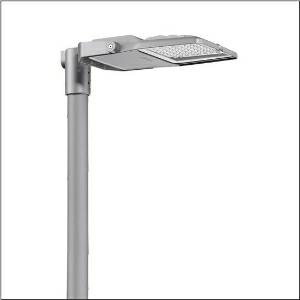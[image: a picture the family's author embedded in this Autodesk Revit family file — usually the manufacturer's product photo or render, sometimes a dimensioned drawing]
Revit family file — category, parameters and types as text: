
# Revit family: floodlight_fl_21_iq_mini___pl43_5xa7772c4a3a_a38e
name_source: partatom
category: Lighting Fixtures
units: mm (PartAtom-declared; Revit-internal decimal feet)

## family parameters
Cut with Voids When Loaded = No
Host = Face
Light Source = No
Part Type = Normal
Room Calculation Point = No
Round Connector Dimension = Use Diameter
Shared = No

## types (1)
- --- (1 x LED, 13050 lm, 87.2 W, 4000K)
    Apparent Load = 87 VA
    CIE Flux Codes = 27 78 99 100 100
    Color Rendering = 70
    Color Temperature = 4000K
    Default Elevation = 1800 mm
    Description = Floodlight FL 21 iQ mini, floodlight, primary light control with lens, of PMMA, primary optical cover: protective disc, of toughened safety glass, transparent, light distribution: PL43, light emission: direct distribution, installation type: surface-mounted, LED, High Power LED, rated luminous flux: 13.050lm, luminous efficacy: 150lm/W, light colour: 740, colour temperature: 4000K, control gear: iQ Street-Remote/DALI, control: Auto-Match, Temp-Guard, Night-Set, Smart-Wire, Desk-Remote (wireless, voltage-free reading and setting of iQ features in the workshop via application-optimized NFC function/RFID function), optimised constant luminous flux control (CLO 2.0), Light-Fading, Lumen-Switch, with terminal, 6-pole, mains connection: 220..240V, AC, 50/60Hz, start of lifetime: 87W, end of service life: 92W, reduction: 40W, luminaire housing, of diecast aluminium, powder-coated, Siteco® metallic grey (DB 702S), corrosivity category C5 mid according to DIN EN ISO 12944, suitable for swimming pools, chlorine-resistant, sealing non-destructively replaceable, please order mast flange separately, mast bracket, of steel, galvanised, powder-coated, protection rating (complete): IP66, insulation class (complete): insulation class II (safety insulation), certification: CE, ENEC, VDE, protection symbol: D, impact resistance: IK08, permissible operating ambient temperature: -40..+40°C, permissible operating ambient temperature for outdoor applications: -40..+50°C, standard: DIN EN 12944, LABS conformity tested according to VDMA 24364:2018-05, packaging unit: 1 piece

Light Distribution: PL43
    Height = 70 mm
    Lamp = 1 x LED
    Lamp Light Flux = 13050 lm
    Lamp Power = 87.2 W
    Lamp count = 1
    Length = 485 mm
    Luminous efficacy = 150 lm/W
    Manufacturer = Siteco
    ModVariant = No
    Model = 5XA7772C4A3A
    Number of Poles = 1
    OnlyDefault = Yes
    Power Factor = 1
    Product Name = Floodlight FL 21 iQ mini | PL43
    Product group = floodlight | pylon annexe
    ProductGroupID = 6200
    Protection Class = Protection class II
    Protection Degree = IP 66
    RLX_Detail_Level = 1
    RLX_Emergency_Light_Flux = 0 lm
    RLX_Emergency_Type = 0
    RLX_Emergency_Type_DB = No
    RlxData = <blob elided: 101397 chars, md5=d3ec095b>
    Socket = socket
    Standby Power = 0 W
    System Light Flux = 13050 lm
    System Power = 87 W
    Type Comments = factory setting: luminous flux: 100 % | dim-lin: 254 | 456 mA
    Type Image = l_1007125.jpg
    URL = http://relux.com
    VarID = @adj_162162
    Voltage = 0 V
    Weight = 0.00 kg
    Width = 337 mm

## geometry (parser evidence)
native form markers: Blend x4, Sweep x13
no freeform markers — native parametric forms only
